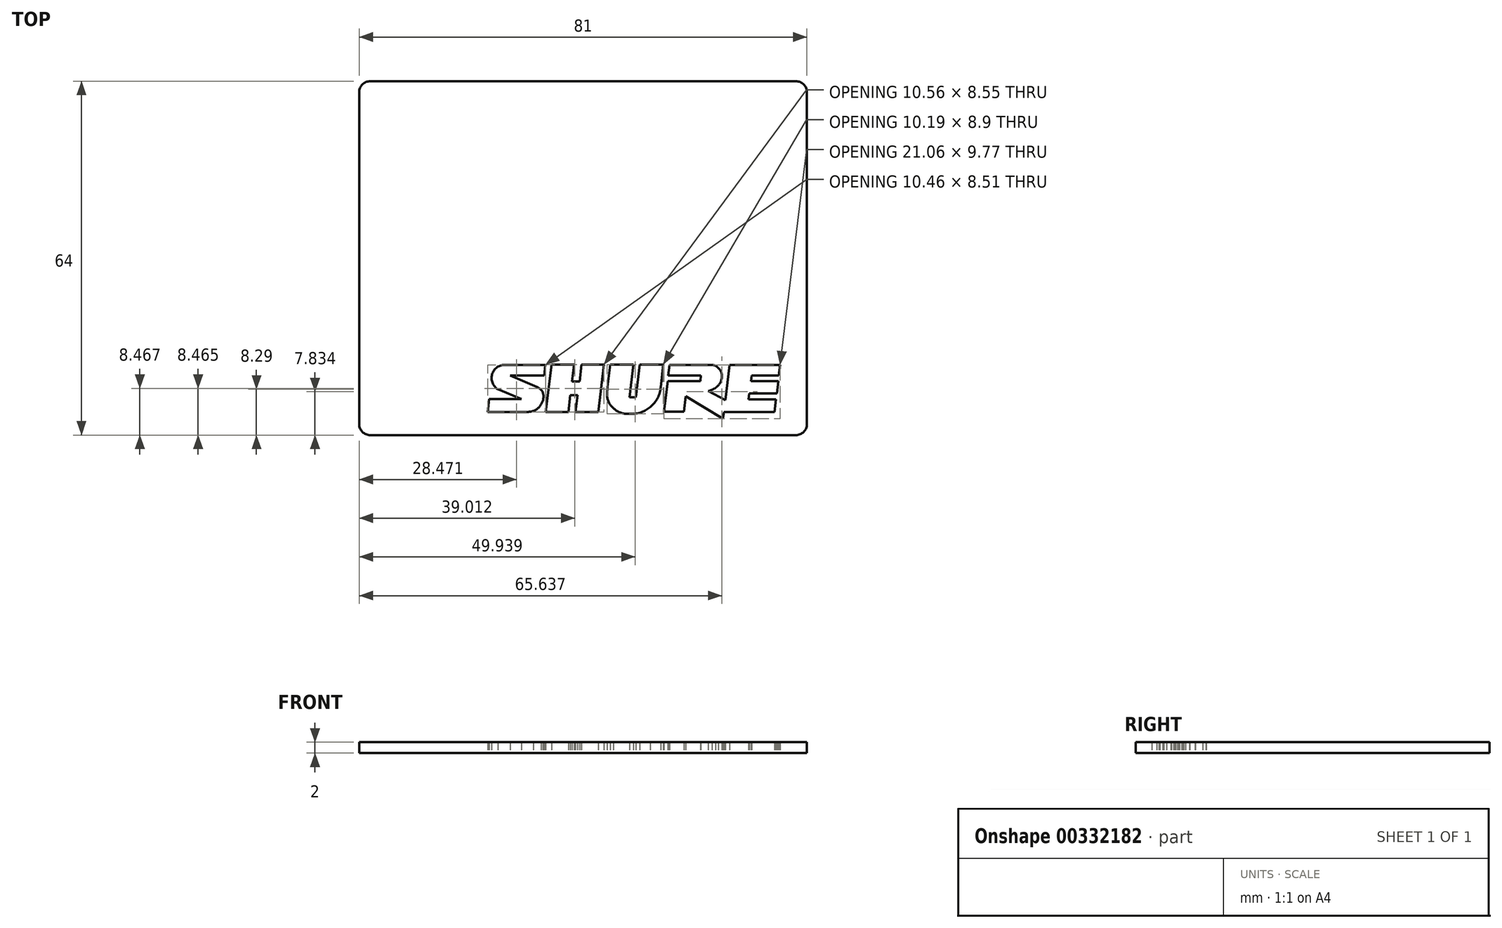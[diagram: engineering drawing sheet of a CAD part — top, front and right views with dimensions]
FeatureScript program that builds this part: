
annotation { "Feature Type Name" : "Feature", "Feature Type Description" : "" }
export const myFeature = defineFeature(function(context is Context, id is Id, definition is map)
    precondition{}
    {
        {
            var Q0;
            Q0=qCreatedBy(makeId("Top.planeOp"),FACE);
            var sketch = newSketch(context, id + "F0", { "sketchPlane" : qUnion([Q0])});
            skLineSegment(sketch, "E0.bottom", {"start": v(-38.5, 32) * mm, "end": v(38.5, 32) * mm});
            skLineSegment(sketch, "E0.top", {"start": v(-38.5, -32) * mm, "end": v(38.5, -32) * mm});
            skLineSegment(sketch, "E0.left", {"start": v(-40.5, 30) * mm, "end": v(-40.5, -30) * mm});
            skLineSegment(sketch, "E0.right", {"start": v(40.5, 30) * mm, "end": v(40.5, -30) * mm});
            skPoint(sketch, "E1.visualSharp", {"position": v(-40.5, 32) * mm});
            skArc(sketch, "E1.filletArc", {"start": v(-38.5, 32) * mm, "mid": v(-39.91, 31.41) * mm, "end": v(-40.5, 30) * mm});
            skPoint(sketch, "E2.visualSharp", {"position": v(-40.5, -32) * mm});
            skArc(sketch, "E2.filletArc", {"start": v(-40.5, -30) * mm, "mid": v(-39.91, -31.41) * mm, "end": v(-38.5, -32) * mm});
            skPoint(sketch, "E3.visualSharp", {"position": v(40.5, -32) * mm});
            skArc(sketch, "E3.filletArc", {"start": v(38.5, -32) * mm, "mid": v(39.91, -31.41) * mm, "end": v(40.5, -30) * mm});
            skPoint(sketch, "E4.visualSharp", {"position": v(40.5, 32) * mm});
            skArc(sketch, "E4.filletArc", {"start": v(40.5, 30) * mm, "mid": v(39.91, 31.41) * mm, "end": v(38.5, 32) * mm});
            skLineSegment(sketch, "E5", {"start": v(-6.8, -19.28) * mm, "end": v(-14.16, -19.28) * mm});
            skLineSegment(sketch, "E6", {"start": v(-6.8, -19.28) * mm, "end": v(-7.04, -21.2) * mm});
            skLineSegment(sketch, "E7", {"start": v(-7.04, -21.2) * mm, "end": v(-13.17, -21.2) * mm});
            skLineSegment(sketch, "E8", {"start": v(-13.17, -21.2) * mm, "end": v(-8.26, -23.34) * mm});
            skLineSegment(sketch, "E9", {"start": v(-11.12, -25.5) * mm, "end": v(-16.98, -25.5) * mm});
            skLineSegment(sketch, "E10", {"start": v(-16.98, -25.5) * mm, "end": v(-17.26, -27.79) * mm});
            skLineSegment(sketch, "E11", {"start": v(-17.26, -27.79) * mm, "end": v(-9.84, -27.79) * mm});
            skLineSegment(sketch, "E12", {"start": v(-15.4, -23.71) * mm, "end": v(-11.12, -25.5) * mm});
            skArc(sketch, "E13", {"start": v(-14.16, -19.28) * mm, "mid": v(-16.46, -21.02) * mm, "end": v(-15.4, -23.71) * mm});
            skArc(sketch, "E14", {"start": v(-7.28, -24.24) * mm, "mid": v(-7.7, -23.7) * mm, "end": v(-8.26, -23.34) * mm});
            skArc(sketch, "E15", {"start": v(-7.58, -26.4) * mm, "mid": v(-7.19, -25.36) * mm, "end": v(-7.28, -24.24) * mm});
            skArc(sketch, "E16", {"start": v(-9, -27.61) * mm, "mid": v(-8.16, -27.15) * mm, "end": v(-7.58, -26.4) * mm});
            skArc(sketch, "E17", {"start": v(-9.84, -27.79) * mm, "mid": v(-9.4, -27.74) * mm, "end": v(-9, -27.61) * mm});
            skLineSegment(sketch, "E18", {"start": v(-5.71, -19.27) * mm, "end": v(-1.61, -19.27) * mm});
            skLineSegment(sketch, "E19", {"start": v(-1.61, -19.27) * mm, "end": v(-2, -22.28) * mm});
            skLineSegment(sketch, "E20", {"start": v(-2, -22.28) * mm, "end": v(-0.6, -22.28) * mm});
            skLineSegment(sketch, "E21", {"start": v(-0.6, -22.28) * mm, "end": v(-0.31, -19.26) * mm});
            skLineSegment(sketch, "E22", {"start": v(-0.31, -19.26) * mm, "end": v(3.79, -19.26) * mm});
            skLineSegment(sketch, "E23", {"start": v(3.79, -19.26) * mm, "end": v(2.73, -27.8) * mm});
            skLineSegment(sketch, "E24", {"start": v(2.73, -27.8) * mm, "end": v(-1.37, -27.8) * mm});
            skLineSegment(sketch, "E25", {"start": v(-1.37, -27.8) * mm, "end": v(-1.02, -24.8) * mm});
            skLineSegment(sketch, "E26", {"start": v(-1.02, -24.8) * mm, "end": v(-2.32, -24.8) * mm});
            skLineSegment(sketch, "E27", {"start": v(-2.32, -24.8) * mm, "end": v(-2.67, -27.8) * mm});
            skLineSegment(sketch, "E28", {"start": v(-2.67, -27.8) * mm, "end": v(-6.77, -27.8) * mm});
            skLineSegment(sketch, "E29", {"start": v(-6.77, -27.8) * mm, "end": v(-5.71, -19.27) * mm});
            skLineSegment(sketch, "E30", {"start": v(4.92, -19.26) * mm, "end": v(9.12, -19.26) * mm});
            skLineSegment(sketch, "E31", {"start": v(9.12, -19.26) * mm, "end": v(8.42, -25.16) * mm});
            skLineSegment(sketch, "E32", {"start": v(8.42, -25.16) * mm, "end": v(9.55, -25.16) * mm});
            skLineSegment(sketch, "E33", {"start": v(9.55, -25.16) * mm, "end": v(10.26, -19.26) * mm});
            skLineSegment(sketch, "E34", {"start": v(10.26, -19.26) * mm, "end": v(14.53, -19.26) * mm});
            skLineSegment(sketch, "E35", {"start": v(14.53, -19.26) * mm, "end": v(14.04, -23.32) * mm});
            skLineSegment(sketch, "E36", {"start": v(4.92, -19.26) * mm, "end": v(4.44, -23.32) * mm});
            skArc(sketch, "E37", {"start": v(12.18, -26.9) * mm, "mid": v(13.48, -25.3) * mm, "end": v(14.04, -23.32) * mm});
            skArc(sketch, "E38", {"start": v(8.65, -28.16) * mm, "mid": v(10.53, -27.86) * mm, "end": v(12.18, -26.9) * mm});
            skLineSegment(sketch, "E39", {"start": v(8.65, -28.16) * mm, "end": v(7.83, -28.14) * mm});
            skArc(sketch, "E40", {"start": v(5.48, -27.12) * mm, "mid": v(6.56, -27.85) * mm, "end": v(7.83, -28.14) * mm});
            skArc(sketch, "E41", {"start": v(4.35, -24.74) * mm, "mid": v(4.65, -26.05) * mm, "end": v(5.48, -27.12) * mm});
            skArc(sketch, "E42", {"start": v(4.44, -23.32) * mm, "mid": v(4.37, -24.03) * mm, "end": v(4.35, -24.74) * mm});
            skLineSegment(sketch, "E43", {"start": v(15.66, -19.28) * mm, "end": v(15.4, -21.23) * mm});
            skLineSegment(sketch, "E44", {"start": v(15.4, -21.23) * mm, "end": v(21.33, -21.23) * mm});
            skLineSegment(sketch, "E45", {"start": v(21.33, -21.23) * mm, "end": v(21.2, -22.25) * mm});
            skLineSegment(sketch, "E46", {"start": v(21.2, -22.25) * mm, "end": v(15.31, -22.25) * mm});
            skLineSegment(sketch, "E47", {"start": v(15.31, -22.25) * mm, "end": v(14.6, -27.78) * mm});
            skLineSegment(sketch, "E48", {"start": v(14.6, -27.78) * mm, "end": v(18.22, -27.78) * mm});
            skLineSegment(sketch, "E49", {"start": v(18.22, -27.78) * mm, "end": v(18.56, -24.96) * mm});
            skLineSegment(sketch, "E50", {"start": v(18.56, -24.96) * mm, "end": v(25.32, -29.05) * mm});
            skLineSegment(sketch, "E51", {"start": v(25.32, -29.05) * mm, "end": v(25.48, -27.8) * mm});
            skLineSegment(sketch, "E52", {"start": v(25.48, -27.8) * mm, "end": v(34.63, -27.8) * mm});
            skLineSegment(sketch, "E53", {"start": v(34.63, -27.8) * mm, "end": v(34.9, -25.54) * mm});
            skLineSegment(sketch, "E54", {"start": v(34.9, -25.54) * mm, "end": v(29.92, -25.54) * mm});
            skLineSegment(sketch, "E55", {"start": v(29.92, -25.54) * mm, "end": v(30.05, -24.42) * mm});
            skLineSegment(sketch, "E56", {"start": v(30.05, -24.42) * mm, "end": v(35.05, -24.42) * mm});
            skLineSegment(sketch, "E57", {"start": v(35.05, -24.42) * mm, "end": v(35.31, -22.25) * mm});
            skLineSegment(sketch, "E58", {"start": v(35.31, -22.25) * mm, "end": v(30.38, -22.25) * mm});
            skLineSegment(sketch, "E59", {"start": v(30.38, -22.25) * mm, "end": v(30.5, -21.24) * mm});
            skLineSegment(sketch, "E60", {"start": v(30.5, -21.24) * mm, "end": v(35.43, -21.24) * mm});
            skLineSegment(sketch, "E61", {"start": v(35.43, -21.24) * mm, "end": v(35.67, -19.29) * mm});
            skLineSegment(sketch, "E62", {"start": v(35.67, -19.29) * mm, "end": v(26.52, -19.29) * mm});
            skLineSegment(sketch, "E63", {"start": v(26.52, -19.29) * mm, "end": v(25.75, -25.64) * mm});
            skLineSegment(sketch, "E64", {"start": v(25.75, -25.64) * mm, "end": v(22.63, -24.04) * mm});
            skLineSegment(sketch, "E65", {"start": v(15.66, -19.28) * mm, "end": v(23.36, -19.28) * mm});
            skArc(sketch, "E66", {"start": v(24.48, -19.85) * mm, "mid": v(23.97, -19.46) * mm, "end": v(23.36, -19.28) * mm});
            skArc(sketch, "E67", {"start": v(25.12, -21.23) * mm, "mid": v(24.95, -20.47) * mm, "end": v(24.48, -19.85) * mm});
            skArc(sketch, "E68", {"start": v(24.48, -22.96) * mm, "mid": v(24.98, -22.16) * mm, "end": v(25.12, -21.23) * mm});
            skArc(sketch, "E69", {"start": v(23.94, -23.47) * mm, "mid": v(24.22, -23.23) * mm, "end": v(24.48, -22.96) * mm});
            skArc(sketch, "E70", {"start": v(22.63, -24.04) * mm, "mid": v(23.31, -23.8) * mm, "end": v(23.94, -23.47) * mm});
            skSolve(sketch);
        }
        {
            var Q0;
            Q0 = qSketchRegion(id + "F0", true);
            extrude(context, id + "F1", {"entities" : qUnion([Q0]), "depth" : 2 * mm});
        }
    });
